FCSTD DOCUMENT  (FreeCAD 0.22R37100 (Git))
Label: composit_stand3_dropper_fix_model
License: All rights reserved
LicenseURL: http://en.wikipedia.org/wiki/All_rights_reserved
objects: App::Link×3, App::DocumentObjectGroup×1, PartDesign::CoordinateSystem×1, App::Part×1
note: 1 computed .brp shape members not serialized (recipe doc carries the construction recipe); baked Part::Feature solids carry a one-line shape summary decoded from their .brp
EXTERNAL_REF file=composit_stand3_dropper_fix_bottom_model.FCStd obj=Local_CS
EXTERNAL_REF file=composit_stand3_dropper_fix_bottom_model.FCStd obj=Body
EXTERNAL_REF file=composit_stand3_dropper_fix_top_model.FCStd obj=Local_CS
EXTERNAL_REF file=composit_stand3_dropper_fix_top_model.FCStd obj=Body
EXTERNAL_REF file=composit_stand3_dropper_fix_fixture_model.FCStd obj=Local_CS
EXTERNAL_REF file=composit_stand3_dropper_fix_fixture_model.FCStd obj=Body

FEATURE [App::DocumentObjectGroup] Parts
FEATURE [PartDesign::CoordinateSystem] LCS_Origin
  AttacherType = Attacher::AttachEngine3D
FEATURE [App::Link] dropper_fix_bottom
  AttachedBy = #Local_CS
  AttachedTo = Parent Assembly#LCS_Origin
  LinkedObject = -> <external composit_stand3_dropper_fix_bottom_model.FCStd>#Body
  SolverId = Asm4EE
  expr: Placement = LCS_Origin.Placement * AttachmentOffset * composit_stand3_dropper_fix_bottom_model#Local_CS.Placement ^ -1
FEATURE [App::Link] dropper_fix_top
  AttachedBy = #Local_CS
  AttachedTo = dropper_fix_bottom#Local_CS
  LinkPlacement = pos=(0,-7e-16,6) rot=(-1,0,0;3.14159rad)
  LinkedObject = -> <external composit_stand3_dropper_fix_top_model.FCStd>#Body
  Placement = pos=(0,-7e-16,6) rot=(-1,0,0;3.14159rad)
  SolverId = Asm4EE
  expr: Placement = dropper_fix_bottom.Placement * composit_stand3_dropper_fix_bottom_model#Local_CS.Placement * AttachmentOffset * Unnamed1#Local_CS.Placement ^ -1
FEATURE [App::Link] dropper_fix_fixture
  AttachedBy = #Local_CS
  AttachedTo = dropper_fix_bottom#Local_CS
  LinkPlacement = pos=(50,0,0) rot=(0,0,1;0rad)
  LinkedObject = -> <external composit_stand3_dropper_fix_fixture_model.FCStd>#Body
  Placement = pos=(50,0,0) rot=(0,0,1;0rad)
  SolverId = Asm4EE
  expr: Placement = dropper_fix_bottom.Placement * composit_stand3_dropper_fix_bottom_model#Local_CS.Placement * AttachmentOffset * Unnamed2#Local_CS.Placement ^ -1
FEATURE [App::Part] Assembly
  AssemblyType = Part::Link
  Group = -> [LCS_Origin,dropper_fix_bottom,dropper_fix_top,dropper_fix_fixture]
  Origin = -> Origin
  Type = Assembly

RESOLVED EXTERNAL PARTS (link-assembly join: the EXTERNAL_REF files above that resolve inside this repo's crawl, each included once):
---- part composit_stand3_dropper_fix_bottom_model.FCStd = doc fcstd_e59e662397be ----
FCSTD DOCUMENT  (FreeCAD 1.1R38827 (Git))
Label: composit_stand3_dropper_fix_bottom_model
License: All rights reserved
LicenseURL: http://en.wikipedia.org/wiki/All_rights_reserved
objects: Part::FeaturePython×9, PartDesign::SubShapeBinder×6, App::Link×4, PartDesign::Pad×3, PartDesign::Body×2, Part::Feature×2, Part::Mirroring×1, Part::Compound×1, Part::MultiFuse×1, PartDesign::Boolean×1, PartDesign::CoordinateSystem×1
note: 34 computed .brp shape members not serialized (recipe doc carries the construction recipe); baked Part::Feature solids carry a one-line shape summary decoded from their .brp
EXTERNAL_REF file=composit_stand3_dropper_fix_main.FCStd obj=Sketch
EXTERNAL_REF file=../dropper.FCStd obj=Sketch007
EXTERNAL_REF file=../dropper.FCStd obj=Part
EXTERNAL_REF file=composit_stand3_dropper_fix_main.FCStd obj=Populate
EXTERNAL_REF file=composit_stand3_dropper_fix_main.FCStd obj=Join
EXTERNAL_REF file=composit_stand3_main.FCStd obj=Cylinder
EXTERNAL_REF file=composit_stand3_dropper_fix_main.FCStd obj=Cylinder

FEATURE [PartDesign::SubShapeBinder] Binder
  BindCopyOnChange = 0
  BindMode = 0
  ClaimChildren = true
  Fuse = false
  MakeFace = true
  OffsetFill = false
  OffsetIntersection = false
  OffsetJoinType = 0
  OffsetOpenResult = false
  PartialLoad = false
  Relative = false
  Support = -> [<external composit_stand3_dropper_fix_main.FCStd>#Sketch]
  _Version = 2
FEATURE [Part::Mirroring] Part__Mirroring  label="Binder (Mirror #1)"
  Base = (0,0,0)
  Normal = (0,1,0)
  Source = -> Binder
FEATURE [Part::FeaturePython] Connect  # WARN: FeaturePython — macro-defined, semantics opaque (R4)
  Objects = -> [Binder,Part__Mirroring]
  Tolerance = 0
FEATURE [PartDesign::SubShapeBinder] Binder001
  BindCopyOnChange = 0
  BindMode = 0
  ClaimChildren = true
  Context = -> Body [Binder001.]
  Fuse = false
  MakeFace = true
  OffsetFill = false
  OffsetIntersection = false
  OffsetJoinType = 0
  OffsetOpenResult = false
  PartialLoad = false
  Relative = false
  Support = -> [Connect]
  _Version = 2
FEATURE [PartDesign::Pad] Pad
  Direction = (0,0,1)
  Length = 3
  Length2 = 10
  Profile = -> Binder001
  Suppressed = false
  Type = 0
FEATURE [PartDesign::SubShapeBinder] Binder002
  BindCopyOnChange = 0
  BindMode = 0
  ClaimChildren = true
  Fuse = false
  MakeFace = true
  OffsetFill = false
  OffsetIntersection = false
  OffsetJoinType = 0
  OffsetOpenResult = false
  PartialLoad = false
  Relative = false
  Support = -> [<external ../dropper.FCStd>#Sketch007]
  _Version = 2
  expr: Support = dropper#<<base>>._self
FEATURE [PartDesign::SubShapeBinder] Binder003
  BindCopyOnChange = 0
  BindMode = 0
  ClaimChildren = true
  Fuse = false
  MakeFace = true
  OffsetFill = false
  OffsetIntersection = false
  OffsetJoinType = 0
  OffsetOpenResult = false
  PartialLoad = false
  Relative = false
  Support = -> [<external ../dropper.FCStd>#Part[Body.Binder.Connect.]]
  _Version = 2
FEATURE [Part::Compound] Compound
  Links = -> [Binder002,Binder003]
FEATURE [Part::FeaturePython] FuseCompound  # WARN: FeaturePython — macro-defined, semantics opaque (R4)
  Base = -> Compound
  Refine = true
  recomputeQuota = -1
FEATURE [PartDesign::SubShapeBinder] Binder004
  BindCopyOnChange = 0
  BindMode = 0
  ClaimChildren = true
  Context = -> Body001 [Binder004.]
  Fuse = false
  MakeFace = true
  OffsetFill = false
  OffsetIntersection = false
  OffsetJoinType = 0
  OffsetOpenResult = false
  PartialLoad = false
  Relative = false
  Support = -> [Binder002]
  _Version = 2
FEATURE [PartDesign::SubShapeBinder] Binder005
  BindCopyOnChange = 0
  BindMode = 0
  ClaimChildren = true
  Context = -> Body001 [Binder005.]
  Fuse = false
  MakeFace = true
  OffsetFill = false
  OffsetIntersection = false
  OffsetJoinType = 0
  OffsetOpenResult = false
  PartialLoad = false
  Placement = pos=(0,0,1.5) rot=(0,0,1;0rad)
  Relative = false
  Support = -> [FuseCompound]
  _Version = 2
FEATURE [PartDesign::Pad] Pad001
  Direction = (0,0,1)
  Length = 10
  Length2 = 10
  Profile = -> Binder004
  Suppressed = false
  Type = 0
FEATURE [PartDesign::Pad] Pad002
  BaseFeature = -> Pad001
  Direction = (0,0,1)
  Length = 10
  Length2 = 10
  Profile = -> Binder005
  Refine = true
  Suppressed = false
  Type = 0
FEATURE [PartDesign::Body] Body001
  AllowCompound = false
  Group = -> [Binder004,Binder005,Pad001,Pad002]
  Origin = -> Origin001
  Tip = -> Pad002
FEATURE [App::Link] Link  label="Populate modules_placement_x with module_dropper"
  LinkedObject = -> <external composit_stand3_dropper_fix_main.FCStd>#Populate
FEATURE [Part::FeaturePython] Mirror  label="Mirror of Populate modules_placement_x with module_dropper"  # WARN: FeaturePython — macro-defined, semantics opaque (R4)
  ExposePlacement = false
  FlipX = false
  FlipY = true
  FlipZ = false
  MarkerShape = 1
  MarkerSize = 0
  NumElements = 4
  Object = -> Link
  ObjectTraversal = 0
  Type = lattice2Mirror.LatticeMirror
  isLattice = 1
FEATURE [Part::FeaturePython] Join  # WARN: FeaturePython — macro-defined, semantics opaque (R4)
  ExposePlacement = false
  Interleave = false
  Links = -> [Link,Mirror]
  MarkerShape = 1
  MarkerSize = 0
  NumElements = 8
  Type = lattice2JoinArrays.JoinArrays
  isLattice = 1
FEATURE [Part::FeaturePython] Populate  label="Populate Join with Body001"  # WARN: FeaturePython — macro-defined, semantics opaque (R4)
  Copying = 0
  ExposePlacement = false
  MarkerShape = 1
  MarkerSize = 0
  NumElements = 0
  Object = -> Body001
  OutputCompounding = 1
  PlacementsTo = -> Join
  Referencing = 0
  Type = lattice2PopulateCopies.LatticePopulateCopies
  isLattice = 0
FEATURE [App::Link] Link001  label="fix"
  LinkedObject = -> <external composit_stand3_dropper_fix_main.FCStd>#Join
FEATURE [App::Link] Link002  label="hole_3.4mm"
  LinkedObject = -> <external composit_stand3_main.FCStd>#Cylinder
FEATURE [Part::FeaturePython] Placment  label="top"  # WARN: FeaturePython — macro-defined, semantics opaque (R4)
  AttacherType = Attacher::AttachEngine3D
  ExposePlacement = true
  MarkerShape = 1
  MarkerSize = 20
  NumElements = 1
  Placement = pos=(0,0,6) rot=(1,0,0;3.14159rad)
  Type = lattice2AttachablePlacement.AttachablePlacement
  isLattice = 1
FEATURE [Part::FeaturePython] Populate002  label="Populate Placment with fix"  # WARN: FeaturePython — macro-defined, semantics opaque (R4)
  Copying = 0
  ExposePlacement = false
  MarkerShape = 1
  MarkerSize = 0
  NumElements = 5
  Object = -> Link001
  OutputCompounding = 0
  PlacementsTo = -> Placment
  Referencing = 0
  Type = lattice2PopulateCopies.LatticePopulateCopies
  isLattice = 1
FEATURE [Part::FeaturePython] Populate001  label="Populate fix with hole_3.4mm"  # WARN: FeaturePython — macro-defined, semantics opaque (R4)
  Copying = 0
  ExposePlacement = false
  MarkerShape = 1
  MarkerSize = 0
  NumElements = 0
  Object = -> Link002
  OutputCompounding = 1
  PlacementsTo = -> Populate002
  Referencing = 0
  Type = lattice2PopulateCopies.LatticePopulateCopies
  isLattice = 0
FEATURE [App::Link] Link003  label="feed_hole"
  LinkTransform = true
  LinkedObject = -> <external composit_stand3_dropper_fix_main.FCStd>#Cylinder
FEATURE [Part::FeaturePython] Populate003  label="Populate top with feed_hole"  # WARN: FeaturePython — macro-defined, semantics opaque (R4)
  Copying = 0
  ExposePlacement = false
  MarkerShape = 1
  MarkerSize = 0
  NumElements = 0
  Object = -> Link003
  OutputCompounding = 2
  PlacementsTo = -> Placment
  Referencing = 0
  Type = lattice2PopulateCopies.LatticePopulateCopies
  isLattice = 0
FEATURE [Part::MultiFuse] Fusion
  Shapes = -> [Populate,Populate001,Populate003]
FEATURE [PartDesign::Boolean] Boolean
  BaseFeature = -> Pad
  Group = -> [Fusion]
  Suppressed = false
  Type = 1
  UsePlacement = true
FEATURE [PartDesign::CoordinateSystem] Local_CS  label="dropper_fix_bottom_LCS"
  AttacherType = Attacher::AttachEngine3D
  AttachmentSupport = -> [XY_Plane]
  MapMode = 5
FEATURE [PartDesign::Body] Body  label="dropper_fix_bottom"
  AllowCompound = false
  Group = -> [Binder001,Pad,Boolean,Local_CS]
  Origin = -> Origin
  Tip = -> Boolean
FEATURE [Part::Feature] Body166  label="dropper_fix_bottom001"
  Placement = pos=(0,0,0) rot=(0,0,-1;1.5708rad)
  shape: bbox 345.1 x 84.2 x 3 mm, 100 faces (baked)
FEATURE [Part::Feature] Body167  label="dropper_fix_top001"
  shape: bbox 84.2 x 342.1 x 3 mm, 109 faces (baked)
---- part composit_stand3_dropper_fix_fixture_model.FCStd = doc fcstd_42cb5ebbac59 ----
FCSTD DOCUMENT  (FreeCAD 1.1R38827 (Git))
Label: composit_stand3_dropper_fix_fixture_model
License: All rights reserved
LicenseURL: http://en.wikipedia.org/wiki/All_rights_reserved
objects: App::Link×4, Part::FeaturePython×3, PartDesign::SubShapeBinder×2, PartDesign::Body×2, PartDesign::FeaturePython×1, Part::MultiFuse×1, PartDesign::Boolean×1, PartDesign::CoordinateSystem×1
note: 13 computed .brp shape members not serialized (recipe doc carries the construction recipe); baked Part::Feature solids carry a one-line shape summary decoded from their .brp
EXTERNAL_REF file=composit_stand3_dropper_fix_fixture_main.FCStd obj=Sketch
EXTERNAL_REF file=composit_stand3_dropper_fix_fixture_main.FCStd obj=Placment
EXTERNAL_REF file=composit_stand3_main.FCStd obj=Cylinder
EXTERNAL_REF file=composit_stand3_dropper_fix_fixture_main.FCStd obj=Join
EXTERNAL_REF file=composit_stand3_dropper_fix_main.FCStd obj=Join

FEATURE [PartDesign::SubShapeBinder] Binder
  BindCopyOnChange = 0
  BindMode = 0
  ClaimChildren = true
  Fuse = false
  MakeFace = true
  OffsetFill = false
  OffsetIntersection = false
  OffsetJoinType = 0
  OffsetOpenResult = false
  PartialLoad = false
  Placement = pos=(0,0,0) rot=(0.57735,0.57735,0.57735;2.0944rad)
  Relative = false
  Support = -> [<external composit_stand3_dropper_fix_fixture_main.FCStd>#Sketch]
  _Version = 2
  expr: Placement = Support[0][0].Placement
FEATURE [PartDesign::SubShapeBinder] Binder001
  BindCopyOnChange = 0
  BindMode = 0
  ClaimChildren = true
  Context = -> Body [Binder001.]
  Fuse = false
  MakeFace = true
  OffsetFill = false
  OffsetIntersection = false
  OffsetJoinType = 0
  OffsetOpenResult = false
  PartialLoad = false
  Placement = pos=(0,0,0) rot=(0.57735,0.57735,0.57735;2.0944rad)
  Relative = false
  Support = -> [Binder]
  _Version = 2
  expr: Placement = Support[0][0].Placement
FEATURE [PartDesign::FeaturePython] BaseBend  # WARN: FeaturePython — macro-defined, semantics opaque (R4)
  BendSide = 1
  BendSketch = -> Binder001
  MidPlane = false
  Reverse = false
  Suppressed = false
  length = 100
  radius = 0.1
  thickness = 0.3
FEATURE [App::Link] Link  label="Placment"
  LinkTransform = true
  LinkedObject = -> <external composit_stand3_dropper_fix_fixture_main.FCStd>#Placment
FEATURE [App::Link] Link001  label="hole_3.4mm"
  LinkedObject = -> <external composit_stand3_main.FCStd>#Cylinder
FEATURE [App::Link] Link002  label="Join"
  LinkedObject = -> <external composit_stand3_dropper_fix_fixture_main.FCStd>#Join
FEATURE [PartDesign::Body] Body001
  AllowCompound = false
  Origin = -> Origin001
FEATURE [App::Link] Link003  label="fix"
  LinkedObject = -> <external composit_stand3_dropper_fix_main.FCStd>#Join
FEATURE [Part::FeaturePython] Populate001  label="Populate Placment with fix"  # WARN: FeaturePython — macro-defined, semantics opaque (R4)
  Copying = 0
  ExposePlacement = false
  MarkerShape = 1
  MarkerSize = 0
  NumElements = 5
  Object = -> Link003
  OutputCompounding = 0
  PlacementsTo = -> Link
  Referencing = 0
  Type = lattice2PopulateCopies.LatticePopulateCopies
  isLattice = 1
FEATURE [Part::FeaturePython] Join  label="Join001"  # WARN: FeaturePython — macro-defined, semantics opaque (R4)
  ExposePlacement = false
  Interleave = false
  Links = -> [Link002,Populate001]
  MarkerShape = 1
  MarkerSize = 0
  NumElements = 15
  Type = lattice2JoinArrays.JoinArrays
  isLattice = 1
FEATURE [Part::FeaturePython] Populate  label="Populate Join with hole_3.4mm"  # WARN: FeaturePython — macro-defined, semantics opaque (R4)
  Copying = 0
  ExposePlacement = false
  MarkerShape = 1
  MarkerSize = 0
  NumElements = 0
  Object = -> Link001
  OutputCompounding = 1
  PlacementsTo = -> Join
  Referencing = 0
  Type = lattice2PopulateCopies.LatticePopulateCopies
  isLattice = 0
FEATURE [Part::MultiFuse] Fusion
  Shapes = -> [Populate]
FEATURE [PartDesign::Boolean] Boolean
  BaseFeature = -> BaseBend
  Group = -> [Fusion]
  Suppressed = false
  Type = 1
  UsePlacement = true
FEATURE [PartDesign::CoordinateSystem] Local_CS
  AttacherType = Attacher::AttachEngine3D
  AttachmentOffset = pos=(-50,0,0) rot=(0,0,1;0rad)
  AttachmentSupport = -> [XY_Plane]
  MapMode = 5
  Placement = pos=(-50,0,0) rot=(0,0,1;0rad)
  expr: .AttachmentOffset.Base.x = <<Placment>>.LinkedObject.Placement.Base.x
FEATURE [PartDesign::Body] Body  label="dropper_fix_fixture"
  AllowCompound = false
  Group = -> [Binder001,BaseBend,Boolean,Local_CS]
  Origin = -> Origin
  Tip = -> Boolean
---- part composit_stand3_dropper_fix_top_model.FCStd = doc fcstd_5f1bdb20550e ----
FCSTD DOCUMENT  (FreeCAD 1.1R38827 (Git))
Label: composit_stand3_dropper_fix_top_model
License: All rights reserved
LicenseURL: http://en.wikipedia.org/wiki/All_rights_reserved
objects: PartDesign::SubShapeBinder×7, Part::FeaturePython×6, App::Link×4, PartDesign::Pad×3, PartDesign::Body×2, Part::Mirroring×1, Part::Compound×1, Part::MultiFuse×1, PartDesign::Boolean×1, PartDesign::CoordinateSystem×1
note: 30 computed .brp shape members not serialized (recipe doc carries the construction recipe); baked Part::Feature solids carry a one-line shape summary decoded from their .brp
EXTERNAL_REF file=composit_stand3_dropper_fix_main.FCStd obj=Sketch
EXTERNAL_REF file=../dropper.FCStd obj=Sketch007
EXTERNAL_REF file=../dropper.FCStd obj=Part
EXTERNAL_REF file=composit_stand3_dropper_fix_main.FCStd obj=Populate
EXTERNAL_REF file=composit_stand3_dropper_fix_main.FCStd obj=Cylinder
EXTERNAL_REF file=composit_stand3_dropper_fix_main.FCStd obj=Join
EXTERNAL_REF file=composit_stand3_main.FCStd obj=Cylinder

FEATURE [PartDesign::SubShapeBinder] Binder
  BindCopyOnChange = 0
  BindMode = 0
  ClaimChildren = true
  Fuse = false
  MakeFace = true
  OffsetFill = false
  OffsetIntersection = false
  OffsetJoinType = 0
  OffsetOpenResult = false
  PartialLoad = false
  Relative = false
  Support = -> [<external composit_stand3_dropper_fix_main.FCStd>#Sketch]
  _Version = 2
FEATURE [Part::Mirroring] Part__Mirroring  label="Binder (Mirror #1)"
  Base = (0,0,0)
  Normal = (0,1,0)
  Source = -> Binder
FEATURE [Part::FeaturePython] Connect  # WARN: FeaturePython — macro-defined, semantics opaque (R4)
  Objects = -> [Binder,Part__Mirroring]
  Tolerance = 0
FEATURE [PartDesign::SubShapeBinder] Binder001
  BindCopyOnChange = 0
  BindMode = 0
  ClaimChildren = true
  Context = -> Body [Binder001.]
  Fuse = false
  MakeFace = true
  OffsetFill = false
  OffsetIntersection = false
  OffsetJoinType = 0
  OffsetOpenResult = false
  PartialLoad = false
  Relative = false
  Support = -> [Connect]
  _Version = 2
FEATURE [PartDesign::SubShapeBinder] Binder002
  BindCopyOnChange = 0
  BindMode = 0
  ClaimChildren = false
  Fuse = false
  MakeFace = true
  OffsetFill = false
  OffsetIntersection = false
  OffsetJoinType = 0
  OffsetOpenResult = false
  PartialLoad = false
  Relative = false
  Support = -> [<external ../dropper.FCStd>#Sketch007]
  _Version = 2
  expr: Support = dropper#<<base>>._self
FEATURE [PartDesign::SubShapeBinder] Binder003
  BindCopyOnChange = 0
  BindMode = 0
  ClaimChildren = false
  Fuse = false
  MakeFace = true
  OffsetFill = false
  OffsetIntersection = false
  OffsetJoinType = 0
  OffsetOpenResult = false
  PartialLoad = false
  Relative = false
  Support = -> [<external ../dropper.FCStd>#Part[Body.Binder.Connect.]]
  _Version = 2
FEATURE [PartDesign::SubShapeBinder] Binder004
  BindCopyOnChange = 0
  BindMode = 0
  ClaimChildren = false
  Fuse = false
  MakeFace = true
  OffsetFill = false
  OffsetIntersection = false
  OffsetJoinType = 0
  OffsetOpenResult = false
  PartialLoad = false
  Relative = true
  Support = -> [<external ../dropper.FCStd>#Part[Body.Sketch008.]]
  _Version = 2
FEATURE [Part::Compound] Compound
  Links = -> [Binder002,Binder003]
FEATURE [Part::FeaturePython] FuseCompound  # WARN: FeaturePython — macro-defined, semantics opaque (R4)
  Base = -> Compound
  Refine = true
  recomputeQuota = -1
FEATURE [PartDesign::SubShapeBinder] Binder005
  BindCopyOnChange = 0
  BindMode = 0
  ClaimChildren = true
  Context = -> Body001 [Binder005.]
  Fuse = false
  MakeFace = true
  OffsetFill = false
  OffsetIntersection = false
  OffsetJoinType = 0
  OffsetOpenResult = false
  PartialLoad = false
  Placement = pos=(0,0,1.5) rot=(0,0,1;0rad)
  Relative = false
  Support = -> [FuseCompound]
  _Version = 2
FEATURE [PartDesign::SubShapeBinder] Binder006
  BindCopyOnChange = 0
  BindMode = 0
  ClaimChildren = true
  Context = -> Body001 [Binder006.]
  Fuse = false
  MakeFace = true
  OffsetFill = false
  OffsetIntersection = false
  OffsetJoinType = 0
  OffsetOpenResult = false
  PartialLoad = false
  Relative = false
  Support = -> [Binder004]
  _Version = 2
FEATURE [PartDesign::Pad] Pad
  Direction = (0,0,1)
  Length = 10
  Length2 = 10
  Profile = -> Binder006
  Suppressed = false
  Type = 0
FEATURE [PartDesign::Pad] Pad001
  BaseFeature = -> Pad
  Direction = (0,0,1)
  Length = 10
  Length2 = 10
  Profile = -> Binder005
  Suppressed = false
  Type = 0
FEATURE [PartDesign::Body] Body001
  AllowCompound = false
  Group = -> [Binder005,Binder006,Pad,Pad001]
  Origin = -> Origin001
  Tip = -> Pad001
FEATURE [PartDesign::Pad] Pad002
  Direction = (0,0,1)
  Length = 3
  Length2 = 10
  Profile = -> Binder001
  Suppressed = false
  Type = 0
FEATURE [App::Link] Link  label="Populate modules_placement_x with module_dropper"
  LinkedObject = -> <external composit_stand3_dropper_fix_main.FCStd>#Populate
FEATURE [Part::FeaturePython] Mirror  label="Mirror of Populate modules_placement_x with module_dropper"  # WARN: FeaturePython — macro-defined, semantics opaque (R4)
  ExposePlacement = false
  FlipX = false
  FlipY = true
  FlipZ = false
  MarkerShape = 1
  MarkerSize = 0
  NumElements = 4
  Object = -> Link
  ObjectTraversal = 0
  Type = lattice2Mirror.LatticeMirror
  isLattice = 1
FEATURE [Part::FeaturePython] Join  # WARN: FeaturePython — macro-defined, semantics opaque (R4)
  ExposePlacement = false
  Interleave = false
  Links = -> [Link,Mirror]
  MarkerShape = 1
  MarkerSize = 0
  NumElements = 8
  Type = lattice2JoinArrays.JoinArrays
  isLattice = 1
FEATURE [Part::FeaturePython] Populate  label="Populate Join with Body001"  # WARN: FeaturePython — macro-defined, semantics opaque (R4)
  Copying = 0
  ExposePlacement = false
  MarkerShape = 1
  MarkerSize = 0
  NumElements = 0
  Object = -> Body001
  OutputCompounding = 1
  PlacementsTo = -> Join
  Referencing = 0
  Type = lattice2PopulateCopies.LatticePopulateCopies
  isLattice = 0
FEATURE [App::Link] Link001  label="feed_hole"
  LinkTransform = true
  LinkedObject = -> <external composit_stand3_dropper_fix_main.FCStd>#Cylinder
FEATURE [App::Link] Link002  label="fix"
  LinkedObject = -> <external composit_stand3_dropper_fix_main.FCStd>#Join
FEATURE [App::Link] Link003  label="hole_3.4mm"
  LinkedObject = -> <external composit_stand3_main.FCStd>#Cylinder
FEATURE [Part::FeaturePython] Populate001  label="Populate fix with hole_3.4mm"  # WARN: FeaturePython — macro-defined, semantics opaque (R4)
  Copying = 0
  ExposePlacement = false
  MarkerShape = 1
  MarkerSize = 0
  NumElements = 0
  Object = -> Link003
  OutputCompounding = 1
  PlacementsTo = -> Link002
  Referencing = 0
  Type = lattice2PopulateCopies.LatticePopulateCopies
  isLattice = 0
FEATURE [Part::MultiFuse] Fusion
  Shapes = -> [Populate,Link001,Populate001]
FEATURE [PartDesign::Boolean] Boolean
  BaseFeature = -> Pad002
  Group = -> [Fusion]
  Suppressed = false
  Type = 1
  UsePlacement = true
FEATURE [PartDesign::CoordinateSystem] Local_CS  label="dropper_fix_top_LCS"
  AttacherType = Attacher::AttachEngine3D
  AttachmentOffset = pos=(0,0,6) rot=(1,0,0;3.14159rad)
  AttachmentSupport = -> [XY_Plane]
  MapMode = 5
  Placement = pos=(0,0,6) rot=(1,0,0;3.14159rad)
FEATURE [PartDesign::Body] Body  label="dropper_fix_top"
  AllowCompound = false
  Group = -> [Binder001,Pad002,Boolean,Local_CS]
  Origin = -> Origin
  Tip = -> Boolean
